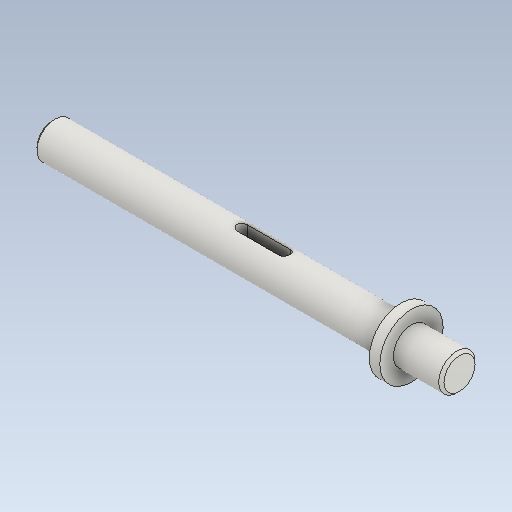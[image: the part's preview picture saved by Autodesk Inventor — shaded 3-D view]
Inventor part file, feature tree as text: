
AUTODESK INVENTOR PART (.ipt)
format: ipt  version: 2021 (Build 250183000, 183)  size: 145,408 bytes
history: native  units: mm
features: other x6, chamfer x2, revolve x1
ambient origin geometry x6: Origin, XZ Plane, XY Plane, X Axis, Y Axis, Z Axis
bodies: Body1 (feature_tree)
feature tree (9):
  other  "Твердое тело1"
  revolve  "Вращение1"
  chamfer  "Фаска3"  [1 undecoded]
  other  "Шпоночный паз1"
  chamfer  "Фаска2"  Distance=6.9mm
  other  "Начальная плоскость"
  other  "Исходная точка"
  other  "Основной эскиз"
  other  "iFeature11:1"
note: 1 required parameter value undecoded (feature->parameter linkage not recoverable at this tier; creation-order binding heuristic only, values carry confidence <= 0.55)
